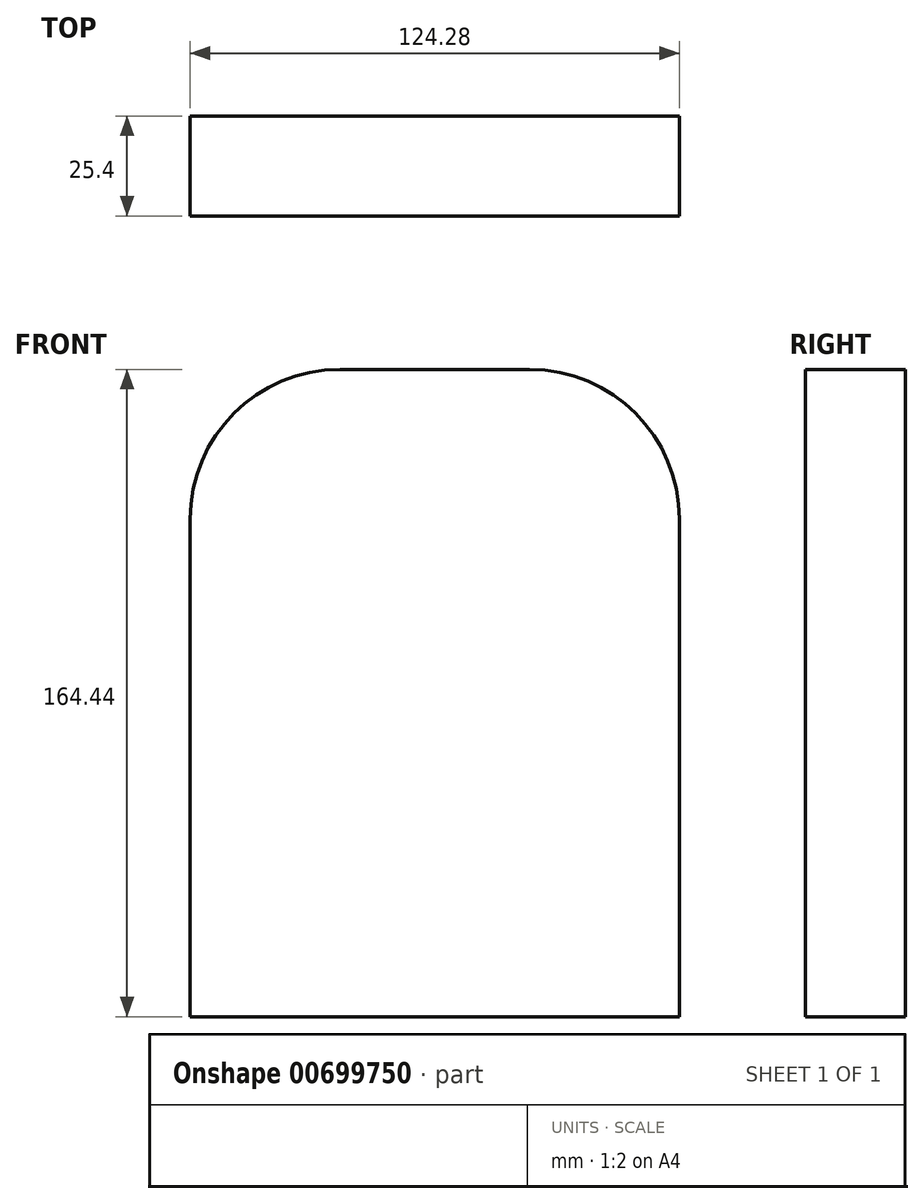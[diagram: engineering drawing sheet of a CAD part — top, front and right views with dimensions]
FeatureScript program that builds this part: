
annotation { "Feature Type Name" : "Feature", "Feature Type Description" : "" }
export const myFeature = defineFeature(function(context is Context, id is Id, definition is map)
    precondition{}
    {
        {
            var Q0;
            Q0=qCreatedBy(makeId("Front.planeOp"),FACE);
            var sketch = newSketch(context, id + "F0", { "sketchPlane" : qUnion([Q0])});
            skLineSegment(sketch, "E0.bottom", {"start": v(-78.52, -86.04) * mm, "end": v(45.76, -86.04) * mm});
            skLineSegment(sketch, "E0.top", {"start": v(-78.52, 78.4) * mm, "end": v(45.76, 78.4) * mm});
            skLineSegment(sketch, "E0.left", {"start": v(-78.52, -86.04) * mm, "end": v(-78.52, 78.4) * mm});
            skLineSegment(sketch, "E0.right", {"start": v(45.76, -86.04) * mm, "end": v(45.76, 78.4) * mm});
            skSolve(sketch);
        }
        {
            var Q0;
            Q0 = qSketchRegion(id + "F0", true);
            extrude(context, id + "F1", {"entities" : qUnion([Q0]), "depth" : 25.4 * mm, "offsetDistance" : 25.4 * mm});
        }
        {
            var Q0;
            Q0=makeQuery(id+"F1.opExtrude","SWEPT_EDGE",EDGE,{"disambiguationData":[OSD([sQuery(id+"F0.wireOp",EDGE,"E0.top"),sQuery(id+"F0.wireOp",EDGE,"E0.left")])]});
            var Q1;
            Q1=makeQuery(id+"F1.opExtrude","SWEPT_EDGE",EDGE,{"disambiguationData":[OSD([sQuery(id+"F0.wireOp",EDGE,"E0.top"),sQuery(id+"F0.wireOp",EDGE,"E0.right")])]});
            fillet(context, id + "F2", {"entities" : qUnion([Q0, Q1]), "radius" : 38.02 * mm, "tangentPropagation" : true, "allowEdgeOverflow" : false});
        }
    });
